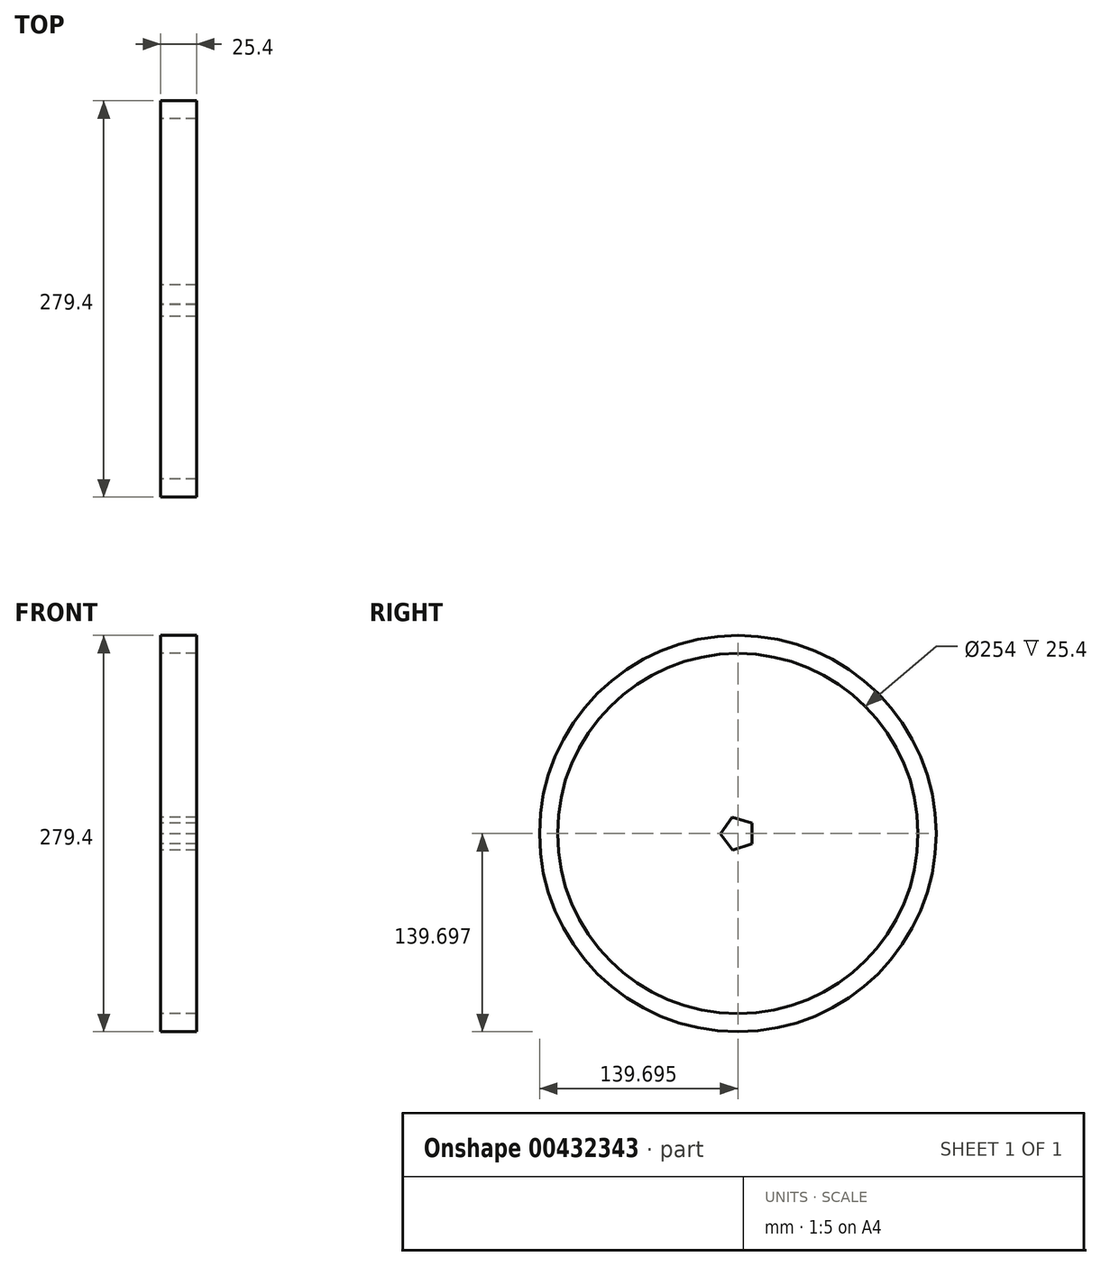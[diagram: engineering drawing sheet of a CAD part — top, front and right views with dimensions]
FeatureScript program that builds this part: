
annotation { "Feature Type Name" : "Feature", "Feature Type Description" : "" }
export const myFeature = defineFeature(function(context is Context, id is Id, definition is map)
    precondition{}
    {
        {
            var Q0;
            Q0=qCreatedBy(makeId("Right.planeOp"),FACE);
            var sketch = newSketch(context, id + "F0", { "sketchPlane" : qUnion([Q0])});
            skCircle(sketch, "E0", {"center": v(-11.36, 38.52) * mm, "radius": 139.7 * mm});
            skCircle(sketch, "E1", {"center": v(-11.36, 38.52) * mm, "radius": 127 * mm});
            skCircle(sketch, "E2.cCircle", {"center": v(-11.36, 38.52) * mm, "radius": 9.96 * mm, "construction": true});
            skLineSegment(sketch, "E2.0", {"start": v(-23.67, 38.33) * mm, "end": v(-15.35, 50.16) * mm});
            skLineSegment(sketch, "E2.1", {"start": v(-15.35, 50.16) * mm, "end": v(-1.52, 45.9) * mm});
            skLineSegment(sketch, "E2.2", {"start": v(-1.52, 45.9) * mm, "end": v(-1.3, 31.44) * mm});
            skLineSegment(sketch, "E2.3", {"start": v(-1.3, 31.44) * mm, "end": v(-14.99, 26.75) * mm});
            skLineSegment(sketch, "E2.4", {"start": v(-14.99, 26.75) * mm, "end": v(-23.67, 38.33) * mm});
            skPoint(sketch, "E2.0.midPoint", {"position": v(-19.51, 44.25) * mm});
            skLineSegment(sketch, "E3", {"start": v(-15.35, 50.16) * mm, "end": v(-110.9, 117.38) * mm});
            skLineSegment(sketch, "E4", {"start": v(-23.67, 38.33) * mm, "end": v(-119.24, 105.55) * mm});
            skLineSegment(sketch, "E5", {"start": v(-15.35, 50.16) * mm, "end": v(19.05, 161.82) * mm});
            skLineSegment(sketch, "E6", {"start": v(-1.52, 45.9) * mm, "end": v(32.88, 157.56) * mm});
            skLineSegment(sketch, "E7", {"start": v(-1.52, 45.9) * mm, "end": v(115.3, 47.7) * mm});
            skLineSegment(sketch, "E8", {"start": v(-1.3, 31.44) * mm, "end": v(115.44, 31.44) * mm});
            skLineSegment(sketch, "E9", {"start": v(-1.3, 31.44) * mm, "end": v(36.5, -79.12) * mm});
            skLineSegment(sketch, "E10", {"start": v(-14.99, 26.75) * mm, "end": v(22.81, -83.8) * mm});
            skLineSegment(sketch, "E11", {"start": v(-23.67, 38.33) * mm, "end": v(-117.13, -31.78) * mm});
            skLineSegment(sketch, "E12", {"start": v(-14.99, 26.75) * mm, "end": v(-108.45, -43.36) * mm});
            skLineSegment(sketch, "E13", {"start": v(-108.45, -43.36) * mm, "end": v(-288.35, 196.45) * mm});
            skSolve(sketch);
        }
        {
            var Q0;
            Q0=makeQuery(id+"F0.imprint","IMPRINT",FACE,{"disambiguationData":[TD([[makeQuery(id+"F0.imprint","IMPRINT",EDGE,{"derivedFrom":sQuery(id+"F0.wireOp",EDGE,"E0")}),1.0]])]});
            var Q1;
            Q1=makeQuery(id+"F0.imprint","IMPRINT",FACE,{"disambiguationData":[TD([[makeQuery(id+"F0.imprint","IMPRINT",EDGE,{"derivedFrom":sQuery(id+"F0.wireOp",EDGE,"E2.0")}),-1.0]])]});
            extrude(context, id + "F1", {"entities" : qUnion([Q0, Q1]), "depth" : 25.4 * mm});
        }
    });
